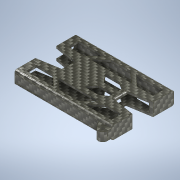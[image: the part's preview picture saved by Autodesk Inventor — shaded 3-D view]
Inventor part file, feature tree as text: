
AUTODESK INVENTOR PART (.ipt)
format: ipt  version: 2020 (Build 240168000, 168)  size: 463,872 bytes
history: native  units: in
note: dims shown in document units (in); Inventor stores cm internally (conversion verified against a paired STEP export)
features: sketch x11, extrude x10, move_body x7, direct_edit x4, fillet x2, revolve x2
ambient origin geometry x8: Origin, YZ Plane, XZ Plane, XY Plane, X Axis, Y Axis, Z Axis, Center Point
bodies: Solid1 (feature_tree)
feature tree (36):
  extrude  "Extrusion1"  Depth=2.1252in
  extrude  "Extrusion2"  Depth=0.0787in
  extrude  "Extrusion3"  Depth=0.4724in TaperAngle=0.0deg
  extrude  "Extrusion4"  Depth=0.761in
  extrude  "Extrusion5"  Depth=0.25in
  sketch  "Sketch6"  dims[d10=0.25in d11=0.25in]
  extrude  "Extrusion6"  Depth=0.25in
  fillet  "Fillet1"  Radius=0.1969in
  revolve  "Revolution1"  [1 undecoded]
  revolve  "Revolution2"  [1 undecoded]
  extrude  "Extrusion7"  Depth=0.1969in
  sketch  "Sketch11"  dims[d26=0.4724in d27=0.0in d28=0.0787in]
  extrude  "Extrusion8"  Depth=0.0787in
  extrude  "Extrusion9"  Depth=0.0787in
  extrude  "Extrusion10"  Depth=0.0787in
  fillet  "Fillet2"  Radius=3.3701in
  direct_edit  "Direct Edit1"
  direct_edit  "Direct Edit2"
  direct_edit  "Direct Edit3"
  sketch  "Sketch12"  dims[d29=0.0787in d30=0.0787in d31=0.0787in d32=3.3701in d33=0.0in d34=0.0394in d35=0.0394in d36=0.7874in d37=0.0in d38=0.0in d39=0.0in d40=0.0394in d41=0.0394in d42=0.0in d43=0.0787in d44=0.3436in d45=0.2749in d46=0.315in d47=0.315in d48=0.0in d49=0.315in d50=0.1181in d51=0.315in d52=0.0in d53=0.315in d54=0.0in d55=0.315in d56=0.0in d57=0.1in d58=0.0in d59=0.0in d60=0.0197in d61=0.0in d62=0.0in d63=0.0197in d64=0.0in d65=0.0in d66=0.0197in d67=0.0in d68=0.0in d69=0.0197in d70=0.0in d71=0.0in d72=0.0197in d73=0.0in d74=0.0in d75=0.0197in d76=0.7874in d77=0.0in d78=0.0in d79=-0.25in]
  direct_edit  "Direct Edit4"
  sketch  "Sketch1"  dims[d0=3.3701in d1=2.1252in]
  sketch  "Sketch2"  dims[d2=0.1181in d3=0.0787in]
  sketch  "Sketch3"  dims[d4=0.0787in d5=0.4724in d6=0.0in]
  sketch  "Sketch5"  dims[d7=0.761in d8=0.761in]
  sketch  "Sketch7"  dims[d13=0.25in d14=0.25in d15=0.1969in]
  sketch  "Sketch8"  dims[d16=0.1969in d17=0.1969in]
  sketch  "Sketch9"  dims[d18=0.1969in d19=0.1969in]
  sketch  "Sketch10"  dims[d23=0.1969in d24=0.1969in]
  move_body  "Move1"
  move_body  "Move2"
  move_body  "Move3"
  move_body  "Move4"
  move_body  "Move5"
  move_body  "Move6"
  move_body  "Move7"
note: 2 required parameter values undecoded (feature->parameter linkage not recoverable at this tier; creation-order binding heuristic only, values carry confidence <= 0.55)
